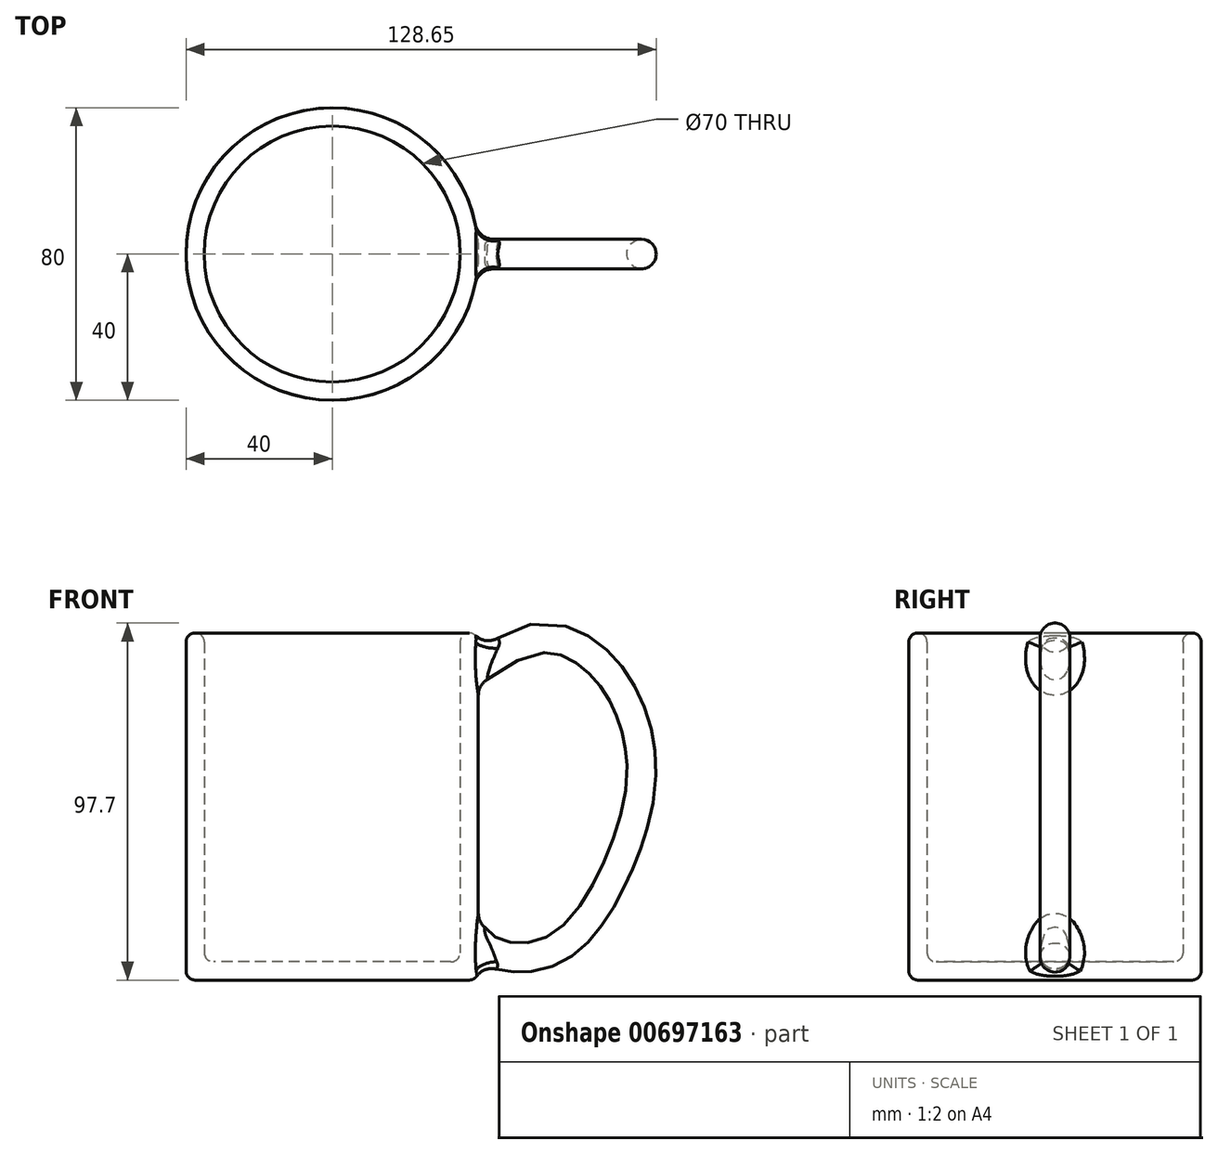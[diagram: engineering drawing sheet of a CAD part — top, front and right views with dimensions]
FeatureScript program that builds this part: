
annotation { "Feature Type Name" : "Feature", "Feature Type Description" : "" }
export const myFeature = defineFeature(function(context is Context, id is Id, definition is map)
    precondition{}
    {
        {
            var Q0;
            Q0=qCreatedBy(makeId("Top.planeOp"),FACE);
            var sketch = newSketch(context, id + "F0", { "sketchPlane" : qUnion([Q0])});
            skCircle(sketch, "E0", {"center": v(0, 0) * mm, "radius": 40 * mm});
            skSolve(sketch);
        }
        {
            var Q0;
            Q0 = qSketchRegion(id + "F0", true);
            extrude(context, id + "F1", {"entities" : qUnion([Q0]), "depth" : 95 * mm, "offsetDistance" : 25 * mm});
        }
        {
            var Q0;
            Q0=qCreatedBy(makeId("Front.planeOp"),FACE);
            var sketch = newSketch(context, id + "F2", { "sketchPlane" : qUnion([Q0])});
            skFitSpline(sketch, "E1", {"points": [v(27.8, 80.82) * mm, v(38.66, 80.61) * mm, v(55.06, 89.56) * mm, v(70.61, 84.02) * mm, v(80.84, 60.38) * mm, v(73.8, 30.56) * mm, v(58.04, 11.17) * mm, v(44.41, 11.6) * mm, v(40.8, 14.8) * mm, v(29.08, 15) * mm], "startDerivative": vector(117.03, -27.02) * mm, "endDerivative": vector(-150.77, -15.06) * mm});
            skSolve(sketch);
        }
        {
            var Q0;
            Q0=qCreatedBy(makeId("Right.planeOp"),FACE);
            cPlane(context, id + "F3", {"entities" : qUnion([Q0]), "cplaneType" : CPlaneType.OFFSET, "offset" : 27.7 * mm, "width" : 150 * mm, "height" : 150 * mm});
        }
        {
            var Q0;
            Q0=qCreatedBy(id+"F3.planeOp",FACE);
            var sketch = newSketch(context, id + "F4", { "sketchPlane" : qUnion([Q0])});
            skCircle(sketch, "E2", {"center": v(0, 84.66) * mm, "radius": 4.08 * mm});
            skSolve(sketch);
        }
        {
            var Q0;
            Q0 = qSketchRegion(id + "F4", true);
            var Q1;
            Q1 = qConstructionFilter(qBodyType(qCreatedBy(id + "F2" ,EDGE), BodyType.WIRE), ConstructionObject.NO);
            sweep(context, id + "F5", {"operationType" : NewBodyOperationType.ADD, "profiles" : qUnion([Q0]), "path" : qUnion([Q1])});
        }
        {
            var Q0;
            Q0=makeQuery(id+"F1.opExtrude","CAP_FACE",FACE,{"disambiguationData":[OSD([sQuery(id+"F0.wireOp",EDGE,"E0")])],"isStart":false});
            shell(context, id + "F6", {"entities" : qUnion([Q0]), "thickness" : 5 * mm});
        }
        {
            var Q0;
            Q0=makeQuery(id+"F1.opExtrude","CAP_FACE",FACE,{"disambiguationData":[OSD([sQuery(id+"F0.wireOp",EDGE,"E0")])],"isStart":false});
            var Q1;
            {var subQ0=sQuery(id+"F0.wireOp",EDGE,"E0");Q1=makeQuery(id+"F6.opShell","OFFSET_EDGE",EDGE,{"disambiguationData":[OSD([subQ0]),TDD([makeQuery(id+"F1.opExtrude","CAP_EDGE",EDGE,{"disambiguationData":[OSD([subQ0])],"isStart":true})])]});}
            var Q2;
            Q2=makeQuery(id+"F1.opExtrude","CAP_EDGE",EDGE,{"disambiguationData":[OSD([sQuery(id+"F0.wireOp",EDGE,"E0")])],"isStart":true});
            var Q3;
            {var subQ0=sQuery(id+"F0.wireOp",EDGE,"E0");Q3=makeQuery(id+"F6.opShell","OFFSET_FACE",FACE,{"disambiguationData":[OSD([subQ0]),TDD([makeQuery(id+"F1.opExtrude","SWEPT_FACE",FACE,{"disambiguationData":[OSD([subQ0])]})])]});}
            fillet(context, id + "F7", {"entities" : qUnion([Q0, Q1, Q2, Q3]), "radius" : 2.5 * mm, "tangentPropagation" : true, "allowEdgeOverflow" : false});
        }
        {
            var Q0;
            Q0=makeQuery(id+"F5.boolean.opBoolean","INTERSECT",EDGE,{"disambiguationData":[OD(1.0)],"derivedFrom":[makeQuery(id+"F1.opExtrude","SWEPT_FACE",FACE,{"disambiguationData":[OSD([sQuery(id+"F0.wireOp",EDGE,"E0")])]}),makeQuery(id+"F5.opSweep","SWEPT_FACE",FACE,{"disambiguationData":[OSD([sQuery(id+"F2.wireOp",EDGE,"E1"),sQuery(id+"F4.wireOp",EDGE,"E2")])]})]});
            var Q1;
            Q1=makeQuery(id+"F5.boolean.opBoolean","INTERSECT",EDGE,{"disambiguationData":[OD(0.0)],"derivedFrom":[makeQuery(id+"F1.opExtrude","SWEPT_FACE",FACE,{"disambiguationData":[OSD([sQuery(id+"F0.wireOp",EDGE,"E0")])]}),makeQuery(id+"F5.opSweep","SWEPT_FACE",FACE,{"disambiguationData":[OSD([sQuery(id+"F2.wireOp",EDGE,"E1"),sQuery(id+"F4.wireOp",EDGE,"E2")])]})]});
            fillet(context, id + "F8", {"entities" : qUnion([Q0, Q1]), "radius" : 5 * mm, "tangentPropagation" : true, "allowEdgeOverflow" : false});
        }
    });
